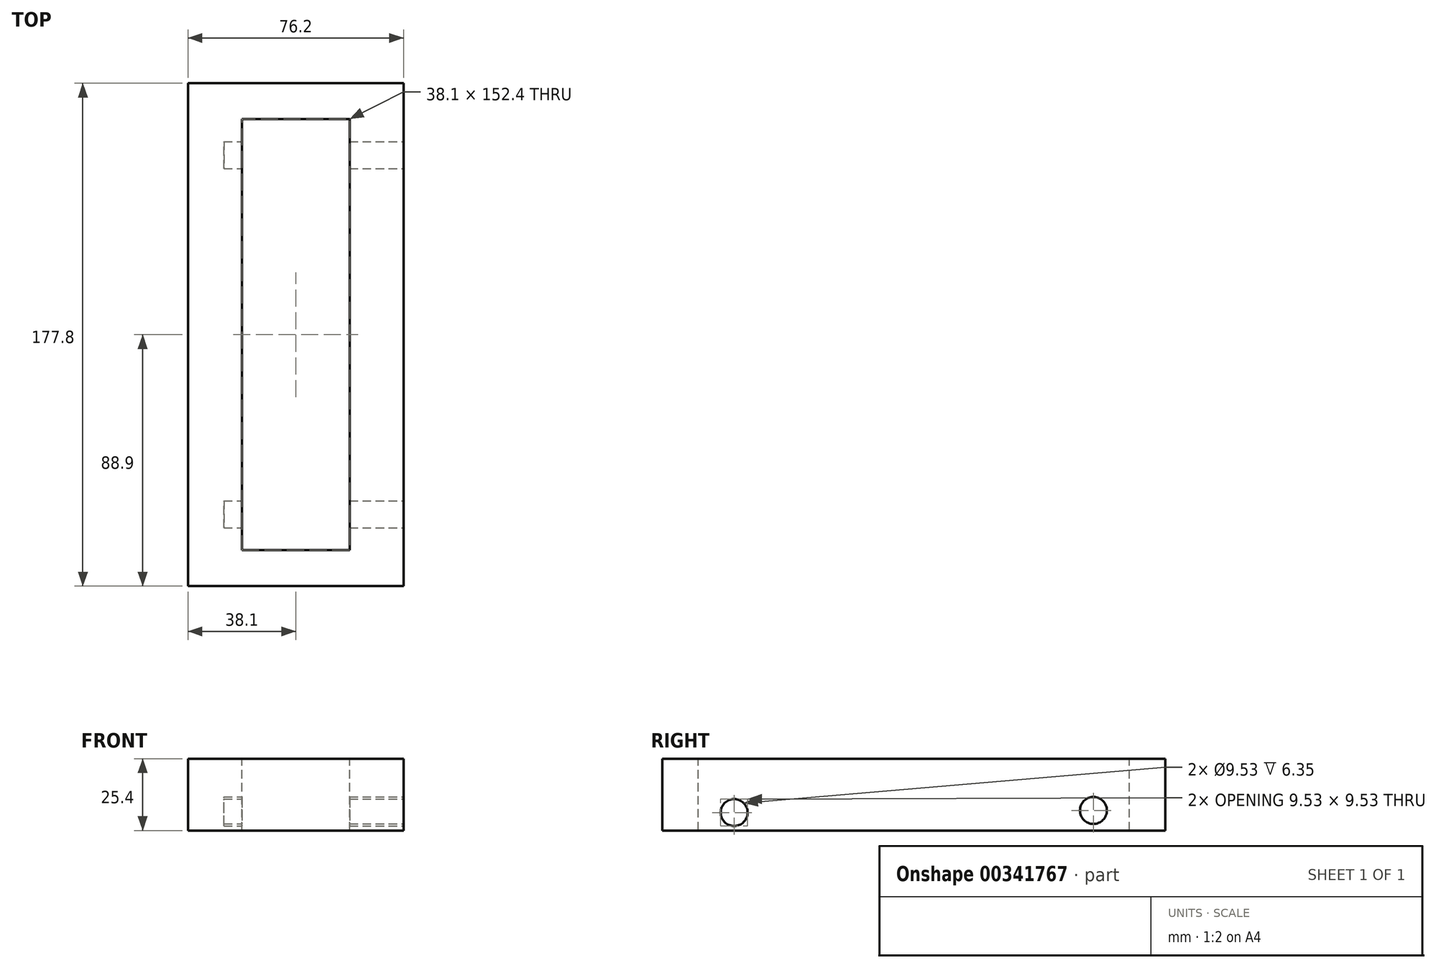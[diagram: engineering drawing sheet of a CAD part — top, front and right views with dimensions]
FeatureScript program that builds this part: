
annotation { "Feature Type Name" : "Feature", "Feature Type Description" : "" }
export const myFeature = defineFeature(function(context is Context, id is Id, definition is map)
    precondition{}
    {
        {
            var Q0;
            Q0=qCreatedBy(makeId("Front.planeOp"),FACE);
            var sketch = newSketch(context, id + "F0", { "sketchPlane" : qUnion([Q0])});
            skLineSegment(sketch, "E0.bottom", {"start": v(-38.1, 12.7) * mm, "end": v(38.1, 12.7) * mm});
            skLineSegment(sketch, "E0.top", {"start": v(-38.1, -12.7) * mm, "end": v(38.1, -12.7) * mm});
            skLineSegment(sketch, "E0.left", {"start": v(-38.1, 12.7) * mm, "end": v(-38.1, -12.7) * mm});
            skLineSegment(sketch, "E0.right", {"start": v(38.1, 12.7) * mm, "end": v(38.1, -12.7) * mm});
            skPoint(sketch, "E0.middle", {"position": v(0, 0) * mm});
            skSolve(sketch);
        }
        {
            var Q0;
            Q0 = qSketchRegion(id + "F0", true);
            extrude(context, id + "F1", {"entities" : qUnion([Q0]), "endBound" : BoundingType.SYMMETRIC, "depth" : 177.8 * mm});
        }
        {
            var Q0;
            Q0=makeQuery(id+"F1.opExtrude","SWEPT_FACE",FACE,{"disambiguationData":[OSD([sQuery(id+"F0.wireOp",EDGE,"E0.bottom")])]});
            var sketch = newSketch(context, id + "F2", { "sketchPlane" : qUnion([Q0])});
            skLineSegment(sketch, "E1.bottom", {"start": v(-19.05, 76.2) * mm, "end": v(19.05, 76.2) * mm});
            skLineSegment(sketch, "E1.top", {"start": v(-19.05, -76.2) * mm, "end": v(19.05, -76.2) * mm});
            skLineSegment(sketch, "E1.left", {"start": v(-19.05, 76.2) * mm, "end": v(-19.05, -76.2) * mm});
            skLineSegment(sketch, "E1.right", {"start": v(19.05, 76.2) * mm, "end": v(19.05, -76.2) * mm});
            skPoint(sketch, "E1.middle", {"position": v(0, 0) * mm});
            skSolve(sketch);
        }
        {
            var Q0;
            Q0 = qSketchRegion(id + "F2", true);
            extrude(context, id + "F3", {"entities" : qUnion([Q0]), "operationType" : NewBodyOperationType.REMOVE, "oppositeDirection" : true, "depth" : 38.1 * mm});
        }
        {
            var Q0;
            Q0=makeQuery(id+"F1.opExtrude","SWEPT_FACE",FACE,{"disambiguationData":[OSD([sQuery(id+"F0.wireOp",EDGE,"E0.right")])]});
            var sketch = newSketch(context, id + "F4", { "sketchPlane" : qUnion([Q0])});
            skLineSegment(sketch, "E2", {"start": v(-63.5, 12.7) * mm, "end": v(-63.5, -12.7) * mm});
            skLineSegment(sketch, "E3", {"start": v(63.5, 12.7) * mm, "end": v(63.5, -12.7) * mm});
            skCircle(sketch, "E4", {"center": v(-63.5, -6.35) * mm, "radius": 4.76 * mm});
            skCircle(sketch, "E5", {"center": v(63.5, -5.61) * mm, "radius": 4.76 * mm});
            skSolve(sketch);
        }
        {
            var Q0;
            {var subQ0=sQuery(id+"F4.wireOp",EDGE,"DjyDW3zc-waUl-Gx8I-x6U5-k15NEP0OEpwc");var subQ1=sQuery(id+"F4.wireOp",EDGE,"E2");var subQ2=makeQuery(id+"F4.imprint","INTERSECT",VERTEX,{"disambiguationData":[OD(0.0)],"derivedFrom":[subQ1,subQ0]});Q0=makeQuery(id+"F4.imprint","IMPRINT",FACE,{"disambiguationData":[TD([[makeQuery(id+"F4.imprint","IMPRINT",EDGE,{"disambiguationData":[TD([[subQ2,-1.0]])],"derivedFrom":subQ1}),1.0]])]});}
            var Q1;
            {var subQ0=sQuery(id+"F4.wireOp",EDGE,"DjyDW3zc-waUl-Gx8I-x6U5-k15NEP0OEpwc");var subQ1=sQuery(id+"F4.wireOp",EDGE,"E2");var subQ2=makeQuery(id+"F4.imprint","INTERSECT",VERTEX,{"disambiguationData":[OD(0.0)],"derivedFrom":[subQ1,subQ0]});Q1=makeQuery(id+"F4.imprint","IMPRINT",FACE,{"disambiguationData":[TD([[makeQuery(id+"F4.imprint","IMPRINT",EDGE,{"disambiguationData":[TD([[subQ2,-1.0]])],"derivedFrom":subQ1}),-1.0]])]});}
            extrude(context, id + "F5", {"entities" : qUnion([Q0, Q1]), "operationType" : NewBodyOperationType.REMOVE, "oppositeDirection" : true, "depth" : 63.5 * mm});
        }
        {
            var Q0;
            {var subQ0=sQuery(id+"F4.wireOp",EDGE,"0OgjKyaV-4nUF-daOL-1tIF-zeGn00FeaVJB");var subQ1=sQuery(id+"F4.wireOp",EDGE,"E3");var subQ2=makeQuery(id+"F4.imprint","INTERSECT",VERTEX,{"disambiguationData":[OD(0.0)],"derivedFrom":[subQ1,subQ0]});Q0=makeQuery(id+"F4.imprint","IMPRINT",FACE,{"disambiguationData":[TD([[makeQuery(id+"F4.imprint","IMPRINT",EDGE,{"disambiguationData":[TD([[subQ2,-1.0]])],"derivedFrom":subQ1}),-1.0]])]});}
            var Q1;
            {var subQ0=sQuery(id+"F4.wireOp",EDGE,"0OgjKyaV-4nUF-daOL-1tIF-zeGn00FeaVJB");var subQ1=sQuery(id+"F4.wireOp",EDGE,"E3");var subQ2=makeQuery(id+"F4.imprint","INTERSECT",VERTEX,{"disambiguationData":[OD(0.0)],"derivedFrom":[subQ1,subQ0]});Q1=makeQuery(id+"F4.imprint","IMPRINT",FACE,{"disambiguationData":[TD([[makeQuery(id+"F4.imprint","IMPRINT",EDGE,{"disambiguationData":[TD([[subQ2,-1.0]])],"derivedFrom":subQ1}),1.0]])]});}
            extrude(context, id + "F6", {"entities" : qUnion([Q0, Q1]), "operationType" : NewBodyOperationType.REMOVE, "oppositeDirection" : true, "depth" : 63.5 * mm});
        }
    });
